# Revit family: Doorset_Porte de bureau sous contrôle d'accès_ASSA ABLOY FR_Hardware LIGHT
name_source: partatom
category: Doors
revit_build: Autodesk Revit 2015 (Build: 20160512_0715(x64)
units: mm (PartAtom-declared; Revit-internal decimal feet)

## types (1)
- 800x2150mm (900x2200mm)
    Architectural Hardware = 1x Béquilles Ovalis 511 _Architectural Hardware_Vachette [AN. 80877 0]
    Assembly Code = C1020
    BIMobject Brand = ASSA ABLOY FR
    BIMobject Category = Doors - Door sets
    BIMobject Product Family = Interior Door Solutions
    BIMobject Product Group = Single-Wood-Access Control
    BIMobject Product Page = http://bimobject.com
    BIMobject Unique ref = ID-ML-EC-FR05
    Clear Height = 2150 mm
    Clear Width = 800 mm  [stored 2.62467 ft]
    Cylinders = 1x APERIO C100_e-cylinder_ASSA ABLOY [AN. 50520190-0001]
    Description = Solution pour porte de bureau, simple vantail, dotée d'un système de contrôle d'accès
    Edition number = 1
    Fire Rating = No
    Frame Depth = 70 mm  [stored 0.229659 ft]
    Frame Height = 2200 mm
    Frame Material = Wood - Assa Abloy - Powder Coated
    Frame Width = 900 mm  [stored 2.95276 ft]
    Function = Interior
    Handle Distance From Side Of The Panel = 50 mm  [stored 0.164042 ft]
    Hardware Set = ID-ML-EC-FR05
    Height = 2200 mm
    IFC classification = Door
    Keynote = 08000
    Lock Cases = 1x Serrure électrique EL564_Electric lock_Abloy [AN. KEL564100440]
    Manufacturer = ASSA ABLOY
    Maximum Door Height = 3000 mm  [stored 9.84252 ft]
    Maximum Door Width = 1200 mm
    Minimum Door Height = 2200 mm
    Minimum Door Width = 900 mm  [stored 2.95276 ft]
    Model = Doorset_Porte de bureau sous contrôle d'accès_ASSA ABLOY FR_Hardware LIGHT
    NBS Reference Code = 59-23
    NBS Reference Description = Doorsets
    Name = Porte de bureau sous contrôle d'accès
    OmniClass Number = 23-17 11 00
    OmniClass Title = Doors
    Panel Height = 2165 mm  [stored 7.10302 ft]
    Panel Material = Wood - Assa Abloy - Powder Coated
    Panel Width = 830 mm
    Product Guid = 51263064-a86c-4632-b4e4-28a220c7b29a
    Provider = ASSA ABLOY FR
    Rough Height = 2210 mm  [stored 7.25066 ft]
    Rough Width = 920 mm
    Side Frame = 70 mm  [stored 0.229659 ft]
    Structural Opening Height = 2210 mm  [stored 7.25066 ft]
    Structural Opening Width = 920 mm
    Thickness = 40 mm  [stored 0.131234 ft]
    Top Frame = 35 mm  [stored 0.114829 ft]
    Type Comments = 800x2150mm (900x2200mm)
    UNSPSC code = 301715
    UNSPSC name = Doors
    URL = http://www.assaabloy.fr
    Uniclass 1.4 Code = JL20
    Uniclass 1.4 Description = Doors
    Uniclass 2.0 Code = PR-59-23
    Uniclass 2.0 Description = Doorsets
    Wall Closure = By host
    Width = 900 mm  [stored 2.95276 ft]

note: [stored X ft] marks values corroborated as IEEE doubles in the binary element streams (Revit-internal decimal feet)

## geometry (parser evidence)
native form markers: Sweep x2
no freeform markers — native parametric forms only
